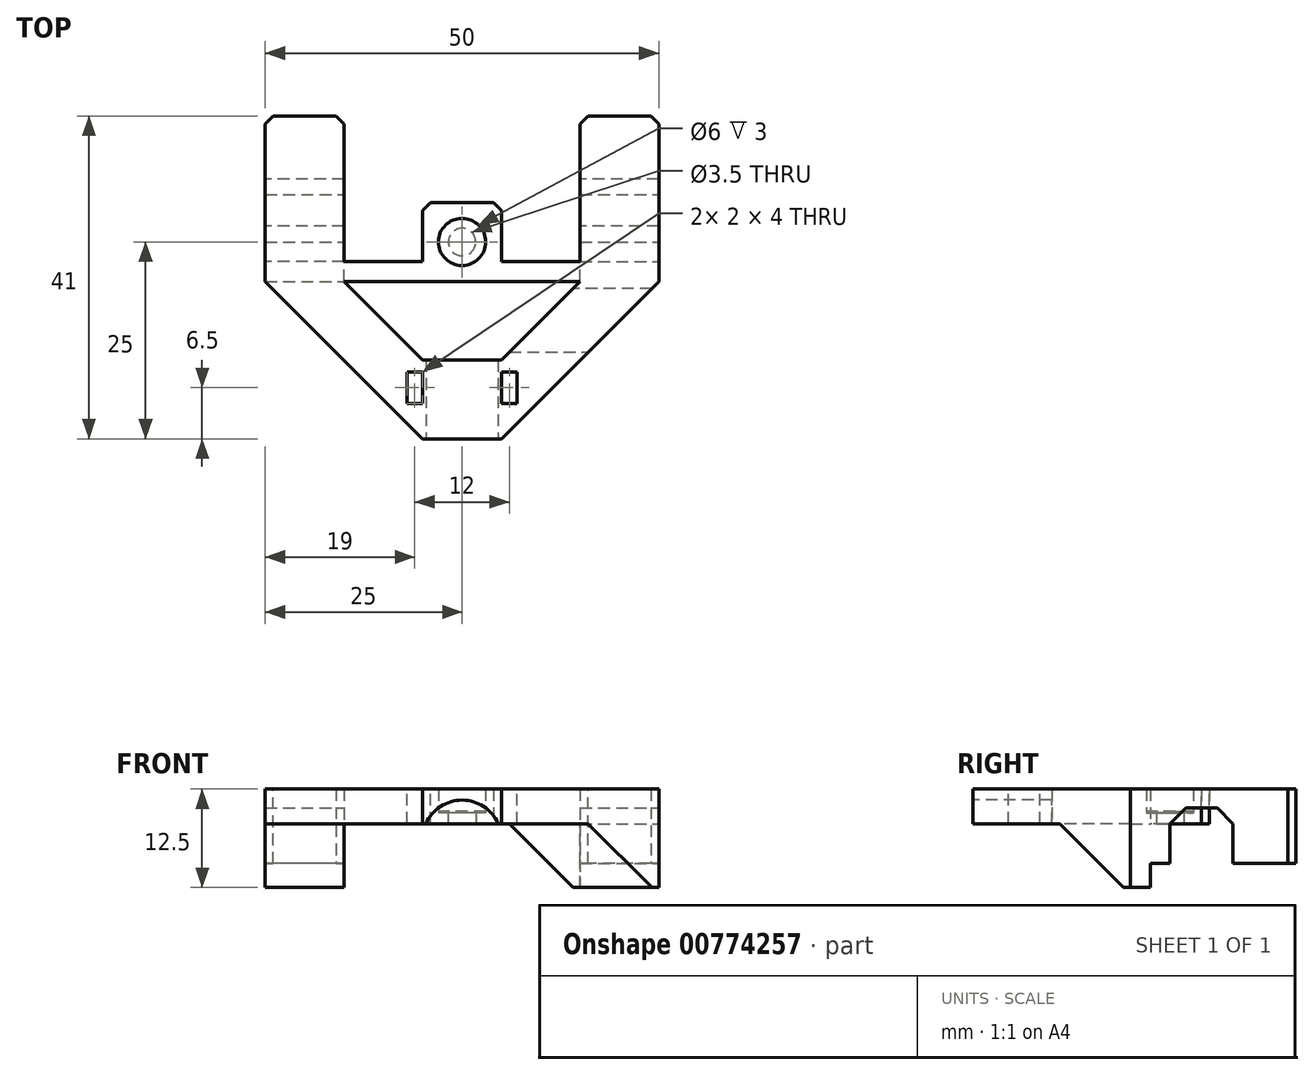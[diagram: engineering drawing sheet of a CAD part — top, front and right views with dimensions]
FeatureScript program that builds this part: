
annotation { "Feature Type Name" : "Feature", "Feature Type Description" : "" }
export const myFeature = defineFeature(function(context is Context, id is Id, definition is map)
    precondition{}
    {
        {
            var Q0;
            Q0=qCreatedBy(makeId("Top.planeOp"),FACE);
            var sketch = newSketch(context, id + "F0", { "sketchPlane" : qUnion([Q0])});
            skCircle(sketch, "E0", {"center": v(0, 0) * mm, "radius": 1.75 * mm});
            skLineSegment(sketch, "E1", {"start": v(0, 0) * mm, "end": v(0, -2.5) * mm, "construction": true});
            skLineSegment(sketch, "E2", {"start": v(0, -2.5) * mm, "end": v(0, -5) * mm, "construction": true});
            skLineSegment(sketch, "E3", {"start": v(0, 0) * mm, "end": v(0, 5) * mm, "construction": true});
            skLineSegment(sketch, "E4.bottom", {"start": v(5, 5) * mm, "end": v(-5, 5) * mm});
            skLineSegment(sketch, "E4.top", {"start": v(5, -5) * mm, "end": v(-5, -5) * mm});
            skLineSegment(sketch, "E4.left", {"start": v(5, 5) * mm, "end": v(5, -5) * mm});
            skLineSegment(sketch, "E4.right", {"start": v(-5, 5) * mm, "end": v(-5, -5) * mm});
            skLineSegment(sketch, "E5", {"start": v(0, -2.5) * mm, "end": v(25, -2.5) * mm, "construction": true});
            skLineSegment(sketch, "E6", {"start": v(0, -2.5) * mm, "end": v(-25, -2.5) * mm, "construction": true});
            skLineSegment(sketch, "E7.bottom", {"start": v(-25, -2.5) * mm, "end": v(-5, -2.5) * mm});
            skLineSegment(sketch, "E7.top", {"start": v(-25, -5) * mm, "end": v(-5, -5) * mm});
            skLineSegment(sketch, "E7.left", {"start": v(-25, -2.5) * mm, "end": v(-25, -5) * mm});
            skLineSegment(sketch, "E7.right", {"start": v(-5, -2.5) * mm, "end": v(-5, -5) * mm});
            skLineSegment(sketch, "E8.bottom", {"start": v(25, -2.5) * mm, "end": v(5, -2.5) * mm});
            skLineSegment(sketch, "E8.top", {"start": v(25, -5) * mm, "end": v(5, -5) * mm});
            skLineSegment(sketch, "E8.left", {"start": v(25, -2.5) * mm, "end": v(25, -5) * mm});
            skLineSegment(sketch, "E8.right", {"start": v(5, -2.5) * mm, "end": v(5, -5) * mm});
            skLineSegment(sketch, "E9.bottom", {"start": v(0, 0) * mm, "end": v(-25, 0) * mm});
            skLineSegment(sketch, "E9.top", {"start": v(0, -2.5) * mm, "end": v(-25, -2.5) * mm});
            skLineSegment(sketch, "E9.left", {"start": v(0, 0) * mm, "end": v(0, -2.5) * mm});
            skLineSegment(sketch, "E9.right", {"start": v(-25, 0) * mm, "end": v(-25, -2.5) * mm});
            skLineSegment(sketch, "E10.bottom", {"start": v(0, 0) * mm, "end": v(25, 0) * mm});
            skLineSegment(sketch, "E10.top", {"start": v(0, -2.5) * mm, "end": v(25, -2.5) * mm});
            skLineSegment(sketch, "E10.right", {"start": v(25, 0) * mm, "end": v(25, -2.5) * mm});
            skLineSegment(sketch, "E11", {"start": v(25, -3.75) * mm, "end": v(15, -3.75) * mm, "construction": true});
            skLineSegment(sketch, "E12", {"start": v(-25, -3.75) * mm, "end": v(-15, -3.75) * mm, "construction": true});
            skLineSegment(sketch, "E13.bottom", {"start": v(-15, -5) * mm, "end": v(-25, -5) * mm});
            skLineSegment(sketch, "E13.top", {"start": v(-15, -2.5) * mm, "end": v(-25, -2.5) * mm});
            skLineSegment(sketch, "E13.left", {"start": v(-15, -5) * mm, "end": v(-15, -2.5) * mm});
            skLineSegment(sketch, "E13.right", {"start": v(-25, -5) * mm, "end": v(-25, -2.5) * mm});
            skLineSegment(sketch, "E14.bottom", {"start": v(15, -5) * mm, "end": v(25, -5) * mm});
            skLineSegment(sketch, "E14.top", {"start": v(15, -2.5) * mm, "end": v(25, -2.5) * mm});
            skLineSegment(sketch, "E14.left", {"start": v(15, -5) * mm, "end": v(15, -2.5) * mm});
            skLineSegment(sketch, "E14.right", {"start": v(25, -5) * mm, "end": v(25, -2.5) * mm});
            skCircle(sketch, "E15", {"center": v(0, 0) * mm, "radius": 3 * mm});
            skLineSegment(sketch, "E16", {"start": v(15, -2.5) * mm, "end": v(15, 0) * mm});
            skLineSegment(sketch, "E17", {"start": v(-15, -2.5) * mm, "end": v(-15, 0) * mm});
            skSolve(sketch);
        }
        {
            var Q0;
            {var subQ1=sQuery(id+"F0.wireOp",EDGE,"E4.top");Q0=makeQuery(id+"F0.imprint","IMPRINT",FACE,{"disambiguationData":[TD([[makeQuery(id+"F0.imprint","IMPRINT",EDGE,{"derivedFrom":subQ1}),-1.0]])]});}
            var Q1;
            {var subQ3=sQuery(id+"F0.wireOp",EDGE,"E10.bottom");var subQ5=sQuery(id+"F0.wireOp",EDGE,"E15");var subQ6=makeQuery(id+"F0.imprint","INTERSECT",VERTEX,{"derivedFrom":[subQ3,subQ5]});Q1=makeQuery(id+"F0.imprint","IMPRINT",FACE,{"disambiguationData":[TD([[makeQuery(id+"F0.imprint","IMPRINT",EDGE,{"disambiguationData":[TD([[subQ6,-1.0]])],"derivedFrom":subQ3}),-1.0]])]});}
            var Q2;
            {var subQ1=sQuery(id+"F0.wireOp",EDGE,"E4.bottom");Q2=makeQuery(id+"F0.imprint","IMPRINT",FACE,{"disambiguationData":[TD([[makeQuery(id+"F0.imprint","IMPRINT",EDGE,{"derivedFrom":subQ1}),1.0]])]});}
            var Q3;
            {var subQ1=sQuery(id+"F0.wireOp",EDGE,"E4.right");var subQ3=sQuery(id+"F0.wireOp",EDGE,"E9.bottom");var subQ4=makeQuery(id+"F0.imprint","INTERSECT",VERTEX,{"derivedFrom":[subQ1,subQ3]});Q3=makeQuery(id+"F0.imprint","IMPRINT",FACE,{"disambiguationData":[TD([[makeQuery(id+"F0.imprint","IMPRINT",EDGE,{"disambiguationData":[TD([[subQ4,1.0]])],"derivedFrom":subQ3}),1.0]])]});}
            extrude(context, id + "F1", {"entities" : qUnion([Q0, Q1, Q2, Q3]), "depth" : 4.4 * mm, "offsetDistance" : 25 * mm});
        }
        {
            var Q0;
            {var subQ0=sQuery(id+"F0.wireOp",EDGE,"E9.right");Q0=makeQuery(id+"F0.imprint","IMPRINT",FACE,{"disambiguationData":[TD([[makeQuery(id+"F0.imprint","IMPRINT",EDGE,{"derivedFrom":subQ0}),1.0]])]});}
            var Q1;
            {var subQ5=sQuery(id+"F0.wireOp",EDGE,"E13.left");Q1=makeQuery(id+"F0.imprint","IMPRINT",FACE,{"disambiguationData":[TD([[makeQuery(id+"F0.imprint","IMPRINT",EDGE,{"derivedFrom":subQ5}),-1.0]])]});}
            var Q2;
            {var subQ5=sQuery(id+"F0.wireOp",EDGE,"E14.left");Q2=makeQuery(id+"F0.imprint","IMPRINT",FACE,{"disambiguationData":[TD([[makeQuery(id+"F0.imprint","IMPRINT",EDGE,{"derivedFrom":subQ5}),1.0]])]});}
            var Q3;
            {var subQ0=sQuery(id+"F0.wireOp",EDGE,"E10.right");Q3=makeQuery(id+"F0.imprint","IMPRINT",FACE,{"disambiguationData":[TD([[makeQuery(id+"F0.imprint","IMPRINT",EDGE,{"derivedFrom":subQ0}),-1.0]])]});}
            var Q4;
            {var subQ0=sQuery(id+"F0.wireOp",EDGE,"E7.left");Q4=makeQuery(id+"F0.imprint","IMPRINT",FACE,{"disambiguationData":[TD([[makeQuery(id+"F0.imprint","IMPRINT",EDGE,{"derivedFrom":subQ0}),1.0]])]});}
            var Q5;
            {var subQ0=sQuery(id+"F0.wireOp",EDGE,"E8.left");Q5=makeQuery(id+"F0.imprint","IMPRINT",FACE,{"disambiguationData":[TD([[makeQuery(id+"F0.imprint","IMPRINT",EDGE,{"derivedFrom":subQ0}),-1.0]])]});}
            extrude(context, id + "F2", {"entities" : qUnion([Q0, Q1, Q2, Q3, Q4, Q5]), "operationType" : NewBodyOperationType.ADD, "depth" : 4.4 * mm, "offsetDistance" : 25 * mm});
        }
        {
            var Q0;
            {var subQ0=sQuery(id+"F0.wireOp",EDGE,"E7.left");Q0=makeQuery(id+"F0.imprint","IMPRINT",FACE,{"disambiguationData":[TD([[makeQuery(id+"F0.imprint","IMPRINT",EDGE,{"derivedFrom":subQ0}),1.0]])]});}
            var Q1;
            {var subQ0=sQuery(id+"F0.wireOp",EDGE,"E8.left");Q1=makeQuery(id+"F0.imprint","IMPRINT",FACE,{"disambiguationData":[TD([[makeQuery(id+"F0.imprint","IMPRINT",EDGE,{"derivedFrom":subQ0}),-1.0]])]});}
            var Q2;
            {var subQ0=sQuery(id+"F0.wireOp",EDGE,"E10.right");Q2=makeQuery(id+"F0.imprint","IMPRINT",FACE,{"disambiguationData":[TD([[makeQuery(id+"F0.imprint","IMPRINT",EDGE,{"derivedFrom":subQ0}),-1.0]])]});}
            var Q3;
            {var subQ0=sQuery(id+"F0.wireOp",EDGE,"E9.right");Q3=makeQuery(id+"F0.imprint","IMPRINT",FACE,{"disambiguationData":[TD([[makeQuery(id+"F0.imprint","IMPRINT",EDGE,{"derivedFrom":subQ0}),1.0]])]});}
            extrude(context, id + "F3", {"entities" : qUnion([Q0, Q1, Q2, Q3]), "operationType" : NewBodyOperationType.ADD, "oppositeDirection" : true, "depth" : 5.05 * mm, "offsetDistance" : 25 * mm});
        }
        {
            var Q0;
            Q0=makeQuery(id+"F3.opExtrude","CAP_FACE",FACE,{"disambiguationData":[OSD([sQuery(id+"F0.wireOp",EDGE,"E8.top"),sQuery(id+"F0.wireOp",EDGE,"E8.left"),sQuery(id+"F0.wireOp",EDGE,"E10.bottom"),sQuery(id+"F0.wireOp",EDGE,"E10.right"),sQuery(id+"F0.wireOp",EDGE,"E14.left"),sQuery(id+"F0.wireOp",EDGE,"E16")])],"isStart":false});
            var sketch = newSketch(context, id + "F4", { "sketchPlane" : qUnion([Q0])});
            skLineSegment(sketch, "E18.0", {"start": v(15, 2.5) * mm, "end": v(25, 2.5) * mm});
            skLineSegment(sketch, "E19.0", {"start": v(0, 0) * mm, "end": v(0, -5) * mm, "construction": true});
            skLineSegment(sketch, "E20.MirrorCS", {"start": v(-15, 2.5) * mm, "end": v(-25, 2.5) * mm});
            skLineSegment(sketch, "E21.0.0", {"start": v(-15, 5) * mm, "end": v(-25, 5) * mm});
            skLineSegment(sketch, "E21.0.1", {"start": v(-25, 5) * mm, "end": v(-25, 0) * mm});
            skLineSegment(sketch, "E21.0.2", {"start": v(-25, 0) * mm, "end": v(-15, 0) * mm});
            skLineSegment(sketch, "E21.0.3", {"start": v(-15, 0) * mm, "end": v(-15, 5) * mm});
            skLineSegment(sketch, "E22.0.0", {"start": v(15, 0) * mm, "end": v(25, 0) * mm});
            skLineSegment(sketch, "E22.0.1", {"start": v(25, 0) * mm, "end": v(25, 5) * mm});
            skLineSegment(sketch, "E22.0.2", {"start": v(25, 5) * mm, "end": v(15, 5) * mm});
            skLineSegment(sketch, "E22.0.3", {"start": v(15, 5) * mm, "end": v(15, 0) * mm});
            skSolve(sketch);
        }
        {
            var Q0;
            {var subQ0=sQuery(id+"F4.wireOp",EDGE,"E18.0");Q0=makeQuery(id+"F4.imprint","IMPRINT",FACE,{"disambiguationData":[TD([[makeQuery(id+"F4.imprint","IMPRINT",EDGE,{"derivedFrom":subQ0}),1.0]])]});}
            var Q1;
            {var subQ0=sQuery(id+"F4.wireOp",EDGE,"E20.MirrorCS");Q1=makeQuery(id+"F4.imprint","IMPRINT",FACE,{"disambiguationData":[TD([[makeQuery(id+"F4.imprint","IMPRINT",EDGE,{"derivedFrom":subQ0}),-1.0]])]});}
            extrude(context, id + "F5", {"entities" : qUnion([Q0, Q1]), "operationType" : NewBodyOperationType.ADD, "depth" : (5.05 - 2) * mm, "offsetDistance" : 25 * mm});
        }
        {
            var Q0;
            Q0=makeQuery(id+"F5.opExtrude","SWEPT_FACE",FACE,{"disambiguationData":[OSD([sQuery(id+"F4.wireOp",EDGE,"E18.0")])]});
            var sketch = newSketch(context, id + "F6", { "sketchPlane" : qUnion([Q0])});
            skLineSegment(sketch, "E23.bottom", {"start": v(-25, -8.1) * mm, "end": v(-15, -8.1) * mm});
            skLineSegment(sketch, "E23.top", {"start": v(-25, -6.3) * mm, "end": v(-15, -6.3) * mm});
            skLineSegment(sketch, "E23.left", {"start": v(-25, -8.1) * mm, "end": v(-25, -6.3) * mm});
            skLineSegment(sketch, "E23.right", {"start": v(-15, -8.1) * mm, "end": v(-15, -6.3) * mm});
            skSolve(sketch);
        }
        {
            var Q0;
            Q0=makeQuery(id+"F5.opExtrude","SWEPT_FACE",FACE,{"disambiguationData":[OSD([sQuery(id+"F4.wireOp",EDGE,"E20.MirrorCS")])]});
            var sketch = newSketch(context, id + "F7", { "sketchPlane" : qUnion([Q0])});
            skLineSegment(sketch, "E24.bottom", {"start": v(15, -8.1) * mm, "end": v(25, -8.1) * mm});
            skLineSegment(sketch, "E24.top", {"start": v(15, -6.3) * mm, "end": v(25, -6.3) * mm});
            skLineSegment(sketch, "E24.left", {"start": v(15, -8.1) * mm, "end": v(15, -6.3) * mm});
            skLineSegment(sketch, "E24.right", {"start": v(25, -8.1) * mm, "end": v(25, -6.3) * mm});
            skSolve(sketch);
        }
        {
            var Q0;
            {var subQ3=sQuery(id+"F0.wireOp",EDGE,"E0");var subQ7=sQuery(id+"F0.wireOp",EDGE,"E9.bottom");var subQ9=makeQuery(id+"F0.imprint","INTERSECT",VERTEX,{"derivedFrom":[subQ3,subQ7]});Q0=makeQuery(id+"F0.imprint","IMPRINT",FACE,{"disambiguationData":[TD([[makeQuery(id+"F0.imprint","IMPRINT",EDGE,{"disambiguationData":[TD([[subQ9,-1.0]])],"derivedFrom":subQ3}),-1.0]])]});}
            var Q1;
            {var subQ0=sQuery(id+"F0.wireOp",EDGE,"E15");var subQ1=sQuery(id+"F0.wireOp",EDGE,"E9.top");var subQ2=makeQuery(id+"F0.imprint","INTERSECT",VERTEX,{"derivedFrom":[subQ1,subQ0]});Q1=makeQuery(id+"F0.imprint","IMPRINT",FACE,{"disambiguationData":[TD([[makeQuery(id+"F0.imprint","IMPRINT",EDGE,{"disambiguationData":[TD([[subQ2,-1.0]])],"derivedFrom":subQ0}),1.0]])]});}
            var Q2;
            {var subQ1=sQuery(id+"F0.wireOp",EDGE,"E10.bottom");var subQ3=sQuery(id+"F0.wireOp",EDGE,"E0");var subQ4=makeQuery(id+"F0.imprint","INTERSECT",VERTEX,{"derivedFrom":[subQ3,subQ1]});Q2=makeQuery(id+"F0.imprint","IMPRINT",FACE,{"disambiguationData":[TD([[makeQuery(id+"F0.imprint","IMPRINT",EDGE,{"disambiguationData":[TD([[subQ4,1.0]])],"derivedFrom":subQ3}),-1.0]])]});}
            var Q3;
            {var subQ0=sQuery(id+"F0.wireOp",EDGE,"E9.bottom");var subQ1=sQuery(id+"F0.wireOp",EDGE,"E0");var subQ2=makeQuery(id+"F0.imprint","INTERSECT",VERTEX,{"derivedFrom":[subQ1,subQ0]});Q3=makeQuery(id+"F0.imprint","IMPRINT",FACE,{"disambiguationData":[TD([[makeQuery(id+"F0.imprint","IMPRINT",EDGE,{"disambiguationData":[TD([[subQ2,1.0]])],"derivedFrom":subQ1}),-1.0]])]});}
            extrude(context, id + "F8", {"entities" : qUnion([Q0, Q1, Q2, Q3]), "operationType" : NewBodyOperationType.ADD, "depth" : 1.4 * mm, "offsetDistance" : 25 * mm});
        }
        {
            var Q0;
            Q0=qCreatedBy(makeId("Top.planeOp"),FACE);
            var sketch = newSketch(context, id + "F9", { "sketchPlane" : qUnion([Q0])});
            skPoint(sketch, "E25.0", {"position": v(-5, -5) * mm});
            skPoint(sketch, "E26.0", {"position": v(5, -5) * mm});
            skPoint(sketch, "E27.0", {"position": v(-25, -5) * mm});
            skPoint(sketch, "E28.0", {"position": v(-15, -5) * mm});
            skPoint(sketch, "E29.0", {"position": v(15, -5) * mm});
            skPoint(sketch, "E30.0", {"position": v(25, -5) * mm});
            skLineSegment(sketch, "E31", {"start": v(-5, -5) * mm, "end": v(-5, -15) * mm, "construction": true});
            skLineSegment(sketch, "E32", {"start": v(5, -5) * mm, "end": v(5, -15) * mm, "construction": true});
            skLineSegment(sketch, "E33", {"start": v(15, -5) * mm, "end": v(15, -15) * mm, "construction": true});
            skLineSegment(sketch, "E34", {"start": v(-15, -5) * mm, "end": v(-15, -15) * mm, "construction": true});
            skLineSegment(sketch, "E35", {"start": v(-15, -5) * mm, "end": v(-5, -15) * mm});
            skLineSegment(sketch, "E36", {"start": v(-5, -15) * mm, "end": v(-5, -25) * mm, "construction": true});
            skLineSegment(sketch, "E37", {"start": v(5, -15) * mm, "end": v(5, -25) * mm, "construction": true});
            skLineSegment(sketch, "E38", {"start": v(-25, -5) * mm, "end": v(-5, -25) * mm});
            skLineSegment(sketch, "E39", {"start": v(-5, -25) * mm, "end": v(5, -25) * mm});
            skLineSegment(sketch, "E40", {"start": v(15, -15) * mm, "end": v(5, -25) * mm});
            skLineSegment(sketch, "E41", {"start": v(25, -5) * mm, "end": v(15, -15) * mm});
            skLineSegment(sketch, "E42", {"start": v(15, -5) * mm, "end": v(5, -15) * mm});
            skLineSegment(sketch, "E43", {"start": v(-5, -15) * mm, "end": v(5, -15) * mm});
            skLineSegment(sketch, "E44", {"start": v(15, -5) * mm, "end": v(25, -5) * mm});
            skLineSegment(sketch, "E45", {"start": v(-25, -5) * mm, "end": v(-15, -5) * mm});
            skSolve(sketch);
        }
        {
            var Q0;
            Q0=makeQuery(id+"F9.imprint","IMPRINT",FACE,{"disambiguationData":[TD([[makeQuery(id+"F9.imprint","IMPRINT",EDGE,{"derivedFrom":sQuery(id+"F9.wireOp",EDGE,"E35")}),-1.0]])]});
            extrude(context, id + "F10", {"entities" : qUnion([Q0]), "operationType" : NewBodyOperationType.ADD, "depth" : 4.4 * mm, "offsetDistance" : 25 * mm});
        }
        {
            var Q0;
            Q0=makeQuery(id+"F10.opExtrude","CAP_EDGE",EDGE,{"disambiguationData":[OSD([sQuery(id+"F9.wireOp",EDGE,"E45")])],"isStart":true});
            var Q1;
            Q1=makeQuery(id+"F10.opExtrude","CAP_EDGE",EDGE,{"disambiguationData":[OSD([sQuery(id+"F9.wireOp",EDGE,"E44")])],"isStart":true});
            chamfer(context, id + "F11", {"entities" : qUnion([Q0, Q1]), "width" : 9 * mm, "tangentPropagation" : true});
        }
        {
            var Q0;
            Q0=makeQuery(id+"FPOSdInb5nQ5QOj_1.boolean.opBoolean","MERGE",FACE,{"derivedFrom":[makeQuery(id+"F10.opExtrude","SWEPT_FACE",FACE,{"disambiguationData":[OSD([sQuery(id+"F9.wireOp",EDGE,"E39")])]}),makeQuery(id+"FPOSdInb5nQ5QOj_1.opExtrude","SWEPT_FACE",FACE,{"disambiguationData":[OSD([sQuery(id+"Fc1zkRG33eWjKpg_1.wireOp",EDGE,"kDbxyCI1-vg0u-zsyr-r6Br-hzq0UtJ8PSwU.top")])]})]});
            var sketch = newSketch(context, id + "F12", { "sketchPlane" : qUnion([Q0])});
            skLineSegment(sketch, "E46", {"start": v(0, 0) * mm, "end": v(0, -2) * mm, "construction": true});
            skCircle(sketch, "E47", {"center": v(0, -2) * mm, "radius": 5 * mm});
            skSolve(sketch);
        }
        {
            var Q0;
            {var subQ0=sQuery(id+"F12.wireOp",EDGE,"E47");var subQ1=makeQuery(id+"F10.opExtrude","CAP_EDGE",EDGE,{"disambiguationData":[OSD([sQuery(id+"F9.wireOp",EDGE,"E39")])],"isStart":true});var subQ2=makeQuery(id+"F12.imprint","INTERSECT",VERTEX,{"disambiguationData":[OD(0.0)],"derivedFrom":[subQ1,subQ0]});Q0=makeQuery(id+"F12.imprint","IMPRINT",FACE,{"disambiguationData":[TD([[makeQuery(id+"F12.imprint","IMPRINT",EDGE,{"disambiguationData":[TD([[subQ2,1.0]])],"derivedFrom":subQ0}),1.0]])]});}
            extrude(context, id + "F13", {"entities" : qUnion([Q0]), "operationType" : NewBodyOperationType.REMOVE, "oppositeDirection" : true, "depth" : 15 * mm, "offsetDistance" : 25 * mm});
        }
        {
            var Q0;
            {var subQ0=sQuery(id+"F0.wireOp",EDGE,"E4.right");var subQ1=sQuery(id+"F0.wireOp",EDGE,"E4.left");Q0=makeQuery(id+"F10.boolean.opBoolean","MERGE",FACE,{"derivedFrom":[makeQuery(id+"F2.boolean.opBoolean","MERGE",FACE,{"derivedFrom":[makeQuery(id+"F1.opExtrude","CAP_FACE",FACE,{"disambiguationData":[OSD([sQuery(id+"F0.wireOp",EDGE,"E4.bottom"),sQuery(id+"F0.wireOp",EDGE,"E4.top"),subQ1,subQ0,sQuery(id+"F0.wireOp",EDGE,"E15")])],"isStart":false}),makeQuery(id+"F2.opExtrude","CAP_FACE",FACE,{"disambiguationData":[OSD([subQ1,sQuery(id+"F0.wireOp",EDGE,"E8.bottom"),sQuery(id+"F0.wireOp",EDGE,"E8.top"),sQuery(id+"F0.wireOp",EDGE,"E8.left"),sQuery(id+"F0.wireOp",EDGE,"E10.bottom"),sQuery(id+"F0.wireOp",EDGE,"E10.right"),sQuery(id+"F0.wireOp",EDGE,"E16")])],"isStart":false}),makeQuery(id+"F2.opExtrude","CAP_FACE",FACE,{"disambiguationData":[OSD([subQ0,sQuery(id+"F0.wireOp",EDGE,"E7.bottom"),sQuery(id+"F0.wireOp",EDGE,"E7.top"),sQuery(id+"F0.wireOp",EDGE,"E7.left"),sQuery(id+"F0.wireOp",EDGE,"E9.bottom"),sQuery(id+"F0.wireOp",EDGE,"E9.right"),sQuery(id+"F0.wireOp",EDGE,"E17")])],"isStart":false})]}),makeQuery(id+"F10.opExtrude","CAP_FACE",FACE,{"disambiguationData":[OSD([sQuery(id+"F9.wireOp",EDGE,"E35"),sQuery(id+"F9.wireOp",EDGE,"E38"),sQuery(id+"F9.wireOp",EDGE,"E39"),sQuery(id+"F9.wireOp",EDGE,"E40"),sQuery(id+"F9.wireOp",EDGE,"E41"),sQuery(id+"F9.wireOp",EDGE,"E42"),sQuery(id+"F9.wireOp",EDGE,"E43"),sQuery(id+"F9.wireOp",EDGE,"E44"),sQuery(id+"F9.wireOp",EDGE,"E45")])],"isStart":false})]});}
            var sketch = newSketch(context, id + "F14", { "sketchPlane" : qUnion([Q0])});
            skPoint(sketch, "E48.0", {"position": v(5, -25) * mm});
            skPoint(sketch, "E49.0", {"position": v(5, -15) * mm});
            skPoint(sketch, "E50.0", {"position": v(-5, -25) * mm});
            skPoint(sketch, "E51.0", {"position": v(-5, -15) * mm});
            skLineSegment(sketch, "E52", {"start": v(5, -25) * mm, "end": v(5, -15) * mm, "construction": true});
            skLineSegment(sketch, "E53", {"start": v(-5, -25) * mm, "end": v(-5, -15) * mm, "construction": true});
            skLineSegment(sketch, "E54", {"start": v(0, -25) * mm, "end": v(0, -15) * mm, "construction": true});
            skLineSegment(sketch, "E55", {"start": v(5, -18.5) * mm, "end": v(-5, -18.5) * mm, "construction": true});
            skLineSegment(sketch, "E56", {"start": v(-5, -18.5) * mm, "end": v(-6, -18.5) * mm, "construction": true});
            skLineSegment(sketch, "E57.bottom", {"start": v(-7, -20.5) * mm, "end": v(-5, -20.5) * mm});
            skLineSegment(sketch, "E57.top", {"start": v(-7, -16.5) * mm, "end": v(-5, -16.5) * mm});
            skLineSegment(sketch, "E57.left", {"start": v(-7, -20.5) * mm, "end": v(-7, -16.5) * mm});
            skLineSegment(sketch, "E57.right", {"start": v(-5, -20.5) * mm, "end": v(-5, -16.5) * mm});
            skPoint(sketch, "E57.middle", {"position": v(-6, -18.5) * mm});
            skLineSegment(sketch, "E58.MirrorCS", {"start": v(5, -20.5) * mm, "end": v(5, -16.5) * mm});
            skLineSegment(sketch, "E59.MirrorCS", {"start": v(7, -20.5) * mm, "end": v(5, -20.5) * mm});
            skLineSegment(sketch, "E60.MirrorCS", {"start": v(7, -20.5) * mm, "end": v(7, -16.5) * mm});
            skLineSegment(sketch, "E61.MirrorCS", {"start": v(7, -16.5) * mm, "end": v(5, -16.5) * mm});
            skSolve(sketch);
        }
        {
            var Q0;
            Q0=makeQuery(id+"F14.imprint","IMPRINT",FACE,{"disambiguationData":[TD([[makeQuery(id+"F14.imprint","IMPRINT",EDGE,{"derivedFrom":sQuery(id+"F14.wireOp",EDGE,"E58.MirrorCS")}),-1.0]])]});
            var Q1;
            Q1=makeQuery(id+"F14.imprint","IMPRINT",FACE,{"disambiguationData":[TD([[makeQuery(id+"F14.imprint","IMPRINT",EDGE,{"derivedFrom":sQuery(id+"F14.wireOp",EDGE,"E57.bottom")}),1.0]])]});
            extrude(context, id + "F15", {"entities" : qUnion([Q0, Q1]), "operationType" : NewBodyOperationType.REMOVE, "oppositeDirection" : true, "depth" : 25 * mm, "offsetDistance" : 25 * mm});
        }
        {
            var Q0;
            {var subQ0=sQuery(id+"F0.wireOp",EDGE,"E9.bottom");Q0=makeQuery(id+"F3.boolean.opBoolean","MERGE",FACE,{"derivedFrom":[makeQuery(id+"F2.opExtrude","SWEPT_FACE",FACE,{"disambiguationData":[OSD([subQ0])]}),makeQuery(id+"F3.opExtrude","SWEPT_FACE",FACE,{"disambiguationData":[OSD([subQ0])]})]});}
            var sketch = newSketch(context, id + "F16", { "sketchPlane" : qUnion([Q0])});
            skLineSegment(sketch, "E62.0", {"start": v(0, 0) * mm, "end": v(25, 0) * mm});
            skLineSegment(sketch, "E63.0", {"start": v(0, 0) * mm, "end": v(-25, 0) * mm});
            skLineSegment(sketch, "E64.0.0", {"start": v(15, 4.4) * mm, "end": v(15, -5.05) * mm});
            skLineSegment(sketch, "E64.0.1", {"start": v(15, -5.05) * mm, "end": v(25, -5.05) * mm});
            skLineSegment(sketch, "E64.0.2", {"start": v(25, -5.05) * mm, "end": v(25, 4.4) * mm});
            skLineSegment(sketch, "E64.0.3", {"start": v(25, 4.4) * mm, "end": v(15, 4.4) * mm});
            skLineSegment(sketch, "E65.0.0", {"start": v(-25, 4.4) * mm, "end": v(-25, -5.05) * mm});
            skLineSegment(sketch, "E65.0.1", {"start": v(-25, -5.05) * mm, "end": v(-15, -5.05) * mm});
            skLineSegment(sketch, "E65.0.2", {"start": v(-15, -5.05) * mm, "end": v(-15, 4.4) * mm});
            skLineSegment(sketch, "E65.0.3", {"start": v(-15, 4.4) * mm, "end": v(-25, 4.4) * mm});
            skSolve(sketch);
        }
        {
            var Q0;
            {var subQ5=sQuery(id+"F16.wireOp",EDGE,"E64.0.3");Q0=makeQuery(id+"F16.imprint","IMPRINT",FACE,{"disambiguationData":[TD([[makeQuery(id+"F16.imprint","IMPRINT",EDGE,{"derivedFrom":subQ5}),-1.0]])]});}
            var Q1;
            {var subQ5=sQuery(id+"F16.wireOp",EDGE,"E65.0.3");Q1=makeQuery(id+"F16.imprint","IMPRINT",FACE,{"disambiguationData":[TD([[makeQuery(id+"F16.imprint","IMPRINT",EDGE,{"derivedFrom":subQ5}),1.0]])]});}
            extrude(context, id + "F17", {"entities" : qUnion([Q0, Q1]), "operationType" : NewBodyOperationType.ADD, "depth" : 16 * mm, "offsetDistance" : 25 * mm});
        }
        {
            var Q0;
            Q0=makeQuery(id+"F17.opExtrude","SWEPT_FACE",FACE,{"disambiguationData":[OSD([sQuery(id+"F16.wireOp",EDGE,"E62.0")])]});
            var sketch = newSketch(context, id + "F18", { "sketchPlane" : qUnion([Q0])});
            skPoint(sketch, "E66.0", {"position": v(25, -8) * mm});
            skPoint(sketch, "E67.0", {"position": v(-25, -8) * mm});
            skLineSegment(sketch, "E68", {"start": v(-25, -8) * mm, "end": v(25, -8) * mm});
            skPoint(sketch, "E69.0", {"position": v(15, -16) * mm});
            skPoint(sketch, "E70.0", {"position": v(-15, -16) * mm});
            skLineSegment(sketch, "E71.bottom", {"start": v(25, -8) * mm, "end": v(15, -8) * mm});
            skLineSegment(sketch, "E71.top", {"start": v(25, -16) * mm, "end": v(15, -16) * mm});
            skLineSegment(sketch, "E71.left", {"start": v(25, -8) * mm, "end": v(25, -16) * mm});
            skLineSegment(sketch, "E71.right", {"start": v(15, -8) * mm, "end": v(15, -16) * mm});
            skLineSegment(sketch, "E72.bottom", {"start": v(-25, -8) * mm, "end": v(-15, -8) * mm});
            skLineSegment(sketch, "E72.top", {"start": v(-25, -16) * mm, "end": v(-15, -16) * mm});
            skLineSegment(sketch, "E72.left", {"start": v(-25, -8) * mm, "end": v(-25, -16) * mm});
            skLineSegment(sketch, "E72.right", {"start": v(-15, -8) * mm, "end": v(-15, -16) * mm});
            skSolve(sketch);
        }
        {
            var Q0;
            Q0=makeQuery(id+"F18.imprint","IMPRINT",FACE,{"disambiguationData":[TD([[makeQuery(id+"F18.imprint","IMPRINT",EDGE,{"derivedFrom":sQuery(id+"F18.wireOp",EDGE,"E72.top")}),-1.0]])]});
            var Q1;
            Q1=makeQuery(id+"F18.imprint","IMPRINT",FACE,{"disambiguationData":[TD([[makeQuery(id+"F18.imprint","IMPRINT",EDGE,{"derivedFrom":sQuery(id+"F18.wireOp",EDGE,"E71.top")}),-1.0]])]});
            extrude(context, id + "F19", {"entities" : qUnion([Q0, Q1]), "operationType" : NewBodyOperationType.ADD, "depth" : 5.05 * mm, "offsetDistance" : 25 * mm});
        }
        {
            var Q0;
            Q0=makeQuery(id+"F17.opExtrude","SWEPT_FACE",FACE,{"disambiguationData":[OSD([sQuery(id+"F16.wireOp",EDGE,"E62.0")])]});
            var Q1;
            Q1=makeQuery(id+"F17.opExtrude","SWEPT_FACE",FACE,{"disambiguationData":[OSD([sQuery(id+"F16.wireOp",EDGE,"E63.0")])]});
            extrude(context, id + "F20", {"entities" : qUnion([Q0, Q1]), "operationType" : NewBodyOperationType.REMOVE, "oppositeDirection" : true, "depth" : 2 * mm, "offsetDistance" : 25 * mm});
        }
        {
            var Q0;
            Q0=makeQuery(id+"F20.boolean.opBoolean","COPY",EDGE,{"derivedFrom":makeQuery(id+"F20.opExtrude","CAP_EDGE",EDGE,{"disambiguationData":[OSD([sQuery(id+"F16.wireOp",EDGE,"E62.0")])],"isStart":false})});
            var Q1;
            {var subQ0=sQuery(id+"F18.wireOp",EDGE,"E68");var subQ1=sQuery(id+"F16.wireOp",EDGE,"E62.0");Q1=makeQuery(id+"F20.boolean.opBoolean","COPY",EDGE,{"derivedFrom":makeQuery(id+"F20.opExtrude","CAP_EDGE",EDGE,{"disambiguationData":[OSD([subQ0]),TDD([makeQuery(id+"F19.opExtrude","CAP_EDGE",EDGE,{"disambiguationData":[OSD([subQ0]),TDD([makeQuery(id+"F18.imprint","IMPRINT",EDGE,{"disambiguationData":[TD([[makeQuery(id+"F18.imprint","INTERSECT",VERTEX,{"derivedFrom":[makeQuery(id+"F17.opExtrude","SWEPT_EDGE",EDGE,{"disambiguationData":[OSD([subQ1,sQuery(id+"F16.wireOp",EDGE,"E64.0.0")])]}),subQ0,sQuery(id+"F18.wireOp",EDGE,"E72.right")]}),1.0]])],"derivedFrom":subQ0})])],"isStart":true})])],"isStart":false})});}
            var Q2;
            Q2=makeQuery(id+"F20.boolean.opBoolean","COPY",EDGE,{"derivedFrom":makeQuery(id+"F20.opExtrude","CAP_EDGE",EDGE,{"disambiguationData":[OSD([sQuery(id+"F16.wireOp",EDGE,"E63.0")])],"isStart":false})});
            var Q3;
            {var subQ0=sQuery(id+"F18.wireOp",EDGE,"E68");Q3=makeQuery(id+"F20.boolean.opBoolean","COPY",EDGE,{"derivedFrom":makeQuery(id+"F20.opExtrude","CAP_EDGE",EDGE,{"disambiguationData":[OSD([subQ0]),TDD([makeQuery(id+"F19.opExtrude","CAP_EDGE",EDGE,{"disambiguationData":[OSD([subQ0]),TDD([makeQuery(id+"F18.imprint","IMPRINT",EDGE,{"disambiguationData":[TD([[makeQuery(id+"F18.imprint","INTERSECT",VERTEX,{"derivedFrom":[subQ0,sQuery(id+"F18.wireOp",EDGE,"E71.left")]}),1.0]])],"derivedFrom":subQ0})])],"isStart":true})])],"isStart":false})});}
            var Q4;
            Q4=makeQuery(id+"F20.boolean.opBoolean","COPY",EDGE,{"derivedFrom":makeQuery(id+"F20.opExtrude","CAP_EDGE",EDGE,{"disambiguationData":[OSD([sQuery(id+"F16.wireOp",EDGE,"E63.0"),sQuery(id+"F16.wireOp",EDGE,"E65.0.2")])],"isStart":false})});
            var Q5;
            Q5=makeQuery(id+"F20.boolean.opBoolean","COPY",EDGE,{"derivedFrom":makeQuery(id+"F20.opExtrude","CAP_EDGE",EDGE,{"disambiguationData":[OSD([sQuery(id+"F16.wireOp",EDGE,"E62.0"),sQuery(id+"F16.wireOp",EDGE,"E64.0.0")])],"isStart":false})});
            var Q6;
            Q6=makeQuery(id+"F20.boolean.opBoolean","COPY",EDGE,{"derivedFrom":makeQuery(id+"F20.opExtrude","CAP_EDGE",EDGE,{"disambiguationData":[OSD([sQuery(id+"F16.wireOp",EDGE,"E63.0"),sQuery(id+"F16.wireOp",EDGE,"E65.0.0")])],"isStart":false})});
            var Q7;
            Q7=makeQuery(id+"F20.boolean.opBoolean","COPY",EDGE,{"derivedFrom":makeQuery(id+"F20.opExtrude","CAP_EDGE",EDGE,{"disambiguationData":[OSD([sQuery(id+"F16.wireOp",EDGE,"E62.0"),sQuery(id+"F16.wireOp",EDGE,"E64.0.2")])],"isStart":false})});
            chamfer(context, id + "F21", {"entities" : qUnion([Q0, Q1, Q2, Q3, Q4, Q5, Q6, Q7]), "width" : 2 * mm, "tangentPropagation" : true});
        }
        {
            var Q0;
            Q0=makeQuery(id+"F1.opExtrude","SWEPT_EDGE",EDGE,{"disambiguationData":[OSD([sQuery(id+"F0.wireOp",EDGE,"E4.bottom"),sQuery(id+"F0.wireOp",EDGE,"E4.left")])]});
            var Q1;
            Q1=makeQuery(id+"F1.opExtrude","SWEPT_EDGE",EDGE,{"disambiguationData":[OSD([sQuery(id+"F0.wireOp",EDGE,"E4.bottom"),sQuery(id+"F0.wireOp",EDGE,"E4.right")])]});
            var Q2;
            {var subQ0=sQuery(id+"F0.wireOp",EDGE,"E10.right");var subQ1=sQuery(id+"F0.wireOp",EDGE,"E10.bottom");Q2=makeQuery(id+"F3.boolean.opBoolean","MERGE",EDGE,{"derivedFrom":[makeQuery(id+"F2.opExtrude","SWEPT_EDGE",EDGE,{"disambiguationData":[OSD([subQ1,subQ0])]}),makeQuery(id+"F3.opExtrude","SWEPT_EDGE",EDGE,{"disambiguationData":[OSD([subQ1,subQ0])]})]});}
            var Q3;
            {var subQ0=sQuery(id+"F0.wireOp",EDGE,"E16");var subQ1=sQuery(id+"F0.wireOp",EDGE,"E10.bottom");Q3=makeQuery(id+"F3.boolean.opBoolean","MERGE",EDGE,{"derivedFrom":[makeQuery(id+"F2.opExtrude","SWEPT_EDGE",EDGE,{"disambiguationData":[OSD([subQ1,subQ0])]}),makeQuery(id+"F3.opExtrude","SWEPT_EDGE",EDGE,{"disambiguationData":[OSD([subQ1,subQ0])]})]});}
            var Q4;
            {var subQ0=sQuery(id+"F0.wireOp",EDGE,"E9.right");var subQ1=sQuery(id+"F0.wireOp",EDGE,"E9.bottom");Q4=makeQuery(id+"F3.boolean.opBoolean","MERGE",EDGE,{"derivedFrom":[makeQuery(id+"F2.opExtrude","SWEPT_EDGE",EDGE,{"disambiguationData":[OSD([subQ1,subQ0])]}),makeQuery(id+"F3.opExtrude","SWEPT_EDGE",EDGE,{"disambiguationData":[OSD([subQ1,subQ0])]})]});}
            var Q5;
            {var subQ0=sQuery(id+"F0.wireOp",EDGE,"E17");var subQ1=sQuery(id+"F0.wireOp",EDGE,"E9.bottom");Q5=makeQuery(id+"F3.boolean.opBoolean","MERGE",EDGE,{"derivedFrom":[makeQuery(id+"F2.opExtrude","SWEPT_EDGE",EDGE,{"disambiguationData":[OSD([subQ1,subQ0])]}),makeQuery(id+"F3.opExtrude","SWEPT_EDGE",EDGE,{"disambiguationData":[OSD([subQ1,subQ0])]})]});}
            var Q6;
            Q6=makeQuery(id+"F19.boolean.opBoolean","MERGE",EDGE,{"derivedFrom":[makeQuery(id+"F17.opExtrude","CAP_EDGE",EDGE,{"disambiguationData":[OSD([sQuery(id+"F16.wireOp",EDGE,"E64.0.2")])],"isStart":false}),makeQuery(id+"F19.opExtrude","SWEPT_EDGE",EDGE,{"disambiguationData":[OSD([sQuery(id+"F18.wireOp",EDGE,"E72.top"),sQuery(id+"F18.wireOp",EDGE,"E72.left")])]})]});
            var Q7;
            Q7=makeQuery(id+"F19.boolean.opBoolean","MERGE",EDGE,{"derivedFrom":[makeQuery(id+"F17.opExtrude","CAP_EDGE",EDGE,{"disambiguationData":[OSD([sQuery(id+"F16.wireOp",EDGE,"E64.0.0")])],"isStart":false}),makeQuery(id+"F19.opExtrude","SWEPT_EDGE",EDGE,{"disambiguationData":[OSD([sQuery(id+"F18.wireOp",EDGE,"E72.top"),sQuery(id+"F18.wireOp",EDGE,"E72.right")])]})]});
            var Q8;
            Q8=makeQuery(id+"F19.boolean.opBoolean","MERGE",EDGE,{"derivedFrom":[makeQuery(id+"F17.opExtrude","CAP_EDGE",EDGE,{"disambiguationData":[OSD([sQuery(id+"F16.wireOp",EDGE,"E65.0.2")])],"isStart":false}),makeQuery(id+"F19.opExtrude","SWEPT_EDGE",EDGE,{"disambiguationData":[OSD([sQuery(id+"F18.wireOp",EDGE,"E71.top"),sQuery(id+"F18.wireOp",EDGE,"E71.right")])]})]});
            var Q9;
            Q9=makeQuery(id+"F19.boolean.opBoolean","MERGE",EDGE,{"derivedFrom":[makeQuery(id+"F17.opExtrude","CAP_EDGE",EDGE,{"disambiguationData":[OSD([sQuery(id+"F16.wireOp",EDGE,"E65.0.0")])],"isStart":false}),makeQuery(id+"F19.opExtrude","SWEPT_EDGE",EDGE,{"disambiguationData":[OSD([sQuery(id+"F18.wireOp",EDGE,"E71.top"),sQuery(id+"F18.wireOp",EDGE,"E71.left")])]})]});
            chamfer(context, id + "F22", {"entities" : qUnion([Q0, Q1, Q2, Q3, Q4, Q5, Q6, Q7, Q8, Q9]), "width" : 1 * mm, "tangentPropagation" : true});
        }
        {
            var Q0;
            Q0=makeQuery(id+"F8.opExtrude","CAP_FACE",FACE,{"disambiguationData":[OSD([sQuery(id+"F0.wireOp",EDGE,"E0"),sQuery(id+"F0.wireOp",EDGE,"E15")])],"isStart":false});
            var sketch = newSketch(context, id + "F23", { "sketchPlane" : qUnion([Q0])});
            skCircle(sketch, "E73.0", {"center": v(0, 0) * mm, "radius": 3 * mm});
            skSolve(sketch);
        }
        {
            var Q0;
            Q0 = qSketchRegion(id + "F23", true);
            var Q1;
            Q1=sQuery(id+"F23.wireOp",EDGE,"E73.0");
            extrude(context, id + "F24", {"entities" : qUnion([Q0]), "surfaceEntities" : qUnion([Q1]), "depth" : 0.15 * mm, "offsetDistance" : 25 * mm});
        }
    });
